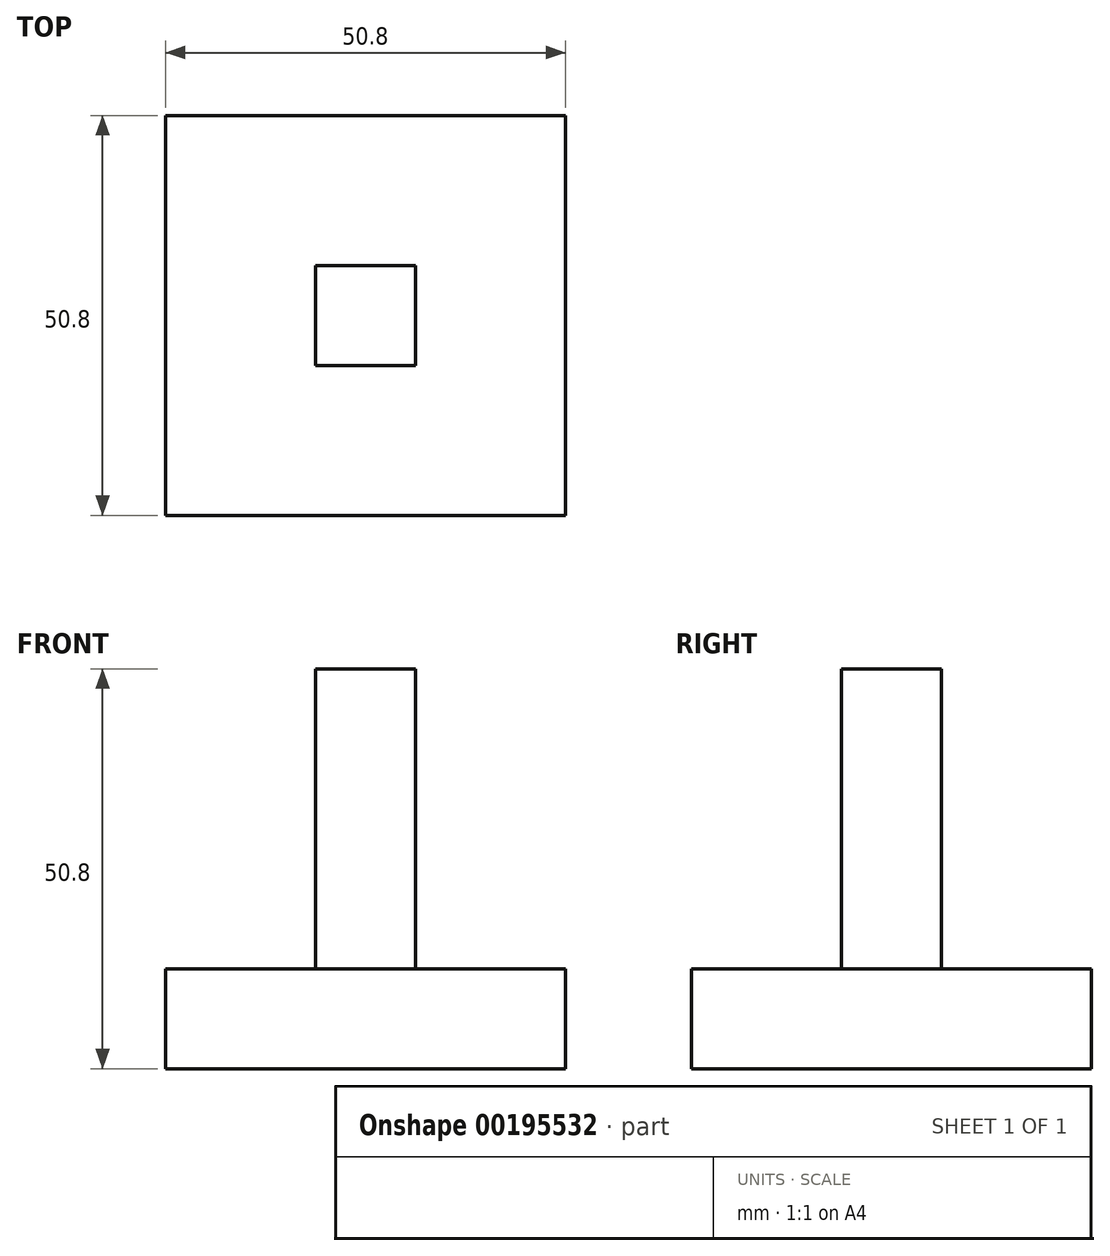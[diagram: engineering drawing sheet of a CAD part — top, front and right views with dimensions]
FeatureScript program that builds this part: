
annotation { "Feature Type Name" : "Feature", "Feature Type Description" : "" }
export const myFeature = defineFeature(function(context is Context, id is Id, definition is map)
    precondition{}
    {
        {
            var Q0;
            Q0=qCreatedBy(makeId("Top.planeOp"),FACE);
            var sketch = newSketch(context, id + "F0", { "sketchPlane" : qUnion([Q0])});
            skLineSegment(sketch, "E0.bottom", {"start": v(-25.4, -25.4) * mm, "end": v(25.4, -25.4) * mm});
            skLineSegment(sketch, "E0.top", {"start": v(-25.4, 25.4) * mm, "end": v(25.4, 25.4) * mm});
            skLineSegment(sketch, "E0.left", {"start": v(-25.4, -25.4) * mm, "end": v(-25.4, 25.4) * mm});
            skLineSegment(sketch, "E0.right", {"start": v(25.4, -25.4) * mm, "end": v(25.4, 25.4) * mm});
            skPoint(sketch, "E0.middle", {"position": v(0, 0) * mm});
            skSolve(sketch);
        }
        {
            var Q0;
            Q0=makeQuery(id+"F0.imprint","IMPRINT",FACE,{"disambiguationData":[TD([[makeQuery(id+"F0.imprint","IMPRINT",EDGE,{"derivedFrom":sQuery(id+"F0.wireOp",EDGE,"E0.bottom")}),1.0]])]});
            extrude(context, id + "F1", {"entities" : qUnion([Q0]), "depth" : 12.7 * mm});
        }
        {
            var Q0;
            Q0=qCreatedBy(makeId("Top.planeOp"),FACE);
            var sketch = newSketch(context, id + "F2", { "sketchPlane" : qUnion([Q0])});
            skLineSegment(sketch, "E1.bottom", {"start": v(-6.35, 6.35) * mm, "end": v(6.35, 6.35) * mm});
            skLineSegment(sketch, "E1.top", {"start": v(-6.35, -6.35) * mm, "end": v(6.35, -6.35) * mm});
            skLineSegment(sketch, "E1.left", {"start": v(-6.35, 6.35) * mm, "end": v(-6.35, -6.35) * mm});
            skLineSegment(sketch, "E1.right", {"start": v(6.35, 6.35) * mm, "end": v(6.35, -6.35) * mm});
            skPoint(sketch, "E1.middle", {"position": v(0, 0) * mm});
            skSolve(sketch);
        }
        {
            var Q0;
            Q0 = qSketchRegion(id + "F2", true);
            extrude(context, id + "F3", {"entities" : qUnion([Q0]), "operationType" : NewBodyOperationType.ADD, "depth" : 50.8 * mm});
        }
    });
